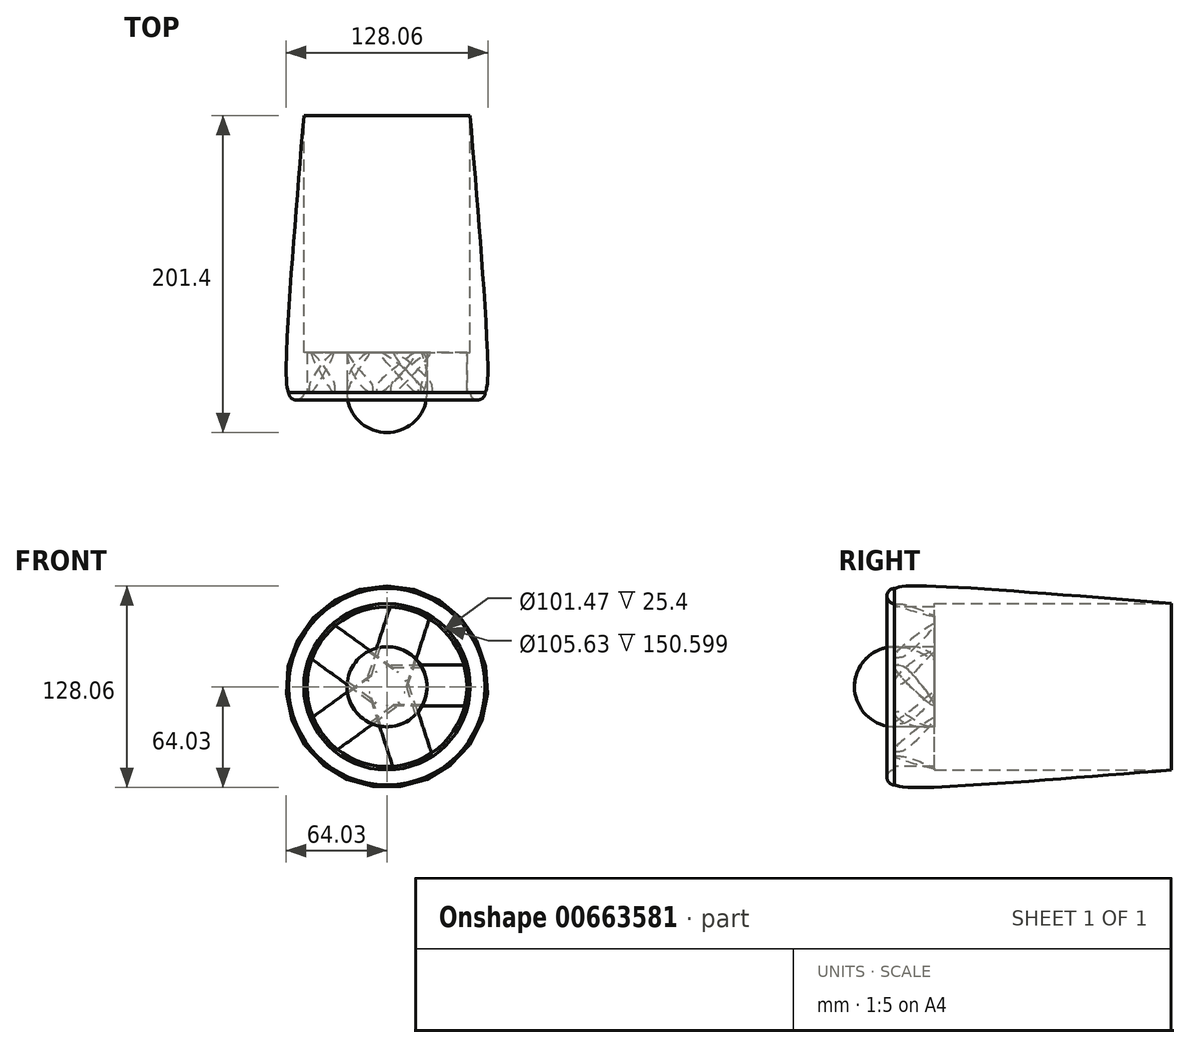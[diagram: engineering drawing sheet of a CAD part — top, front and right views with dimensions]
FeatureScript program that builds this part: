
annotation { "Feature Type Name" : "Feature", "Feature Type Description" : "" }
export const myFeature = defineFeature(function(context is Context, id is Id, definition is map)
    precondition{}
    {
        {
            var Q0;
            Q0=qCreatedBy(makeId("Front.planeOp"),FACE);
            var sketch = newSketch(context, id + "F0", { "sketchPlane" : qUnion([Q0])});
            skCircle(sketch, "E0", {"center": v(0, 0) * mm, "radius": 25.4 * mm});
            skSolve(sketch);
        }
        {
            var Q0;
            Q0 = qSketchRegion(id + "F0", true);
            extrude(context, id + "F1", {"entities" : qUnion([Q0]), "oppositeDirection" : true, "depth" : 25.4 * mm, "offsetDistance" : 25.4 * mm});
        }
        {
            var Q0;
            Q0=qCreatedBy(makeId("Right.planeOp"),FACE);
            var sketch = newSketch(context, id + "F2", { "sketchPlane" : qUnion([Q0])});
            skLineSegment(sketch, "E1", {"start": v(-7.86, -12.08) * mm, "end": v(25.4, -12.08) * mm, "construction": true});
            skLineSegment(sketch, "E2", {"start": v(25.4, -12.08) * mm, "end": v(1.25, 12.07) * mm, "construction": true});
            skLineSegment(sketch, "E3", {"start": v(1.25, 12.07) * mm, "end": v(1.25, -12.08) * mm, "construction": true});
            skFitSpline(sketch, "E4", {"points": [v(0, 13.64) * mm, v(2.87, 13.72) * mm, v(7.87, 11.5) * mm, v(25.4, -12.08) * mm, v(2.79, 7.92) * mm, v(0, 13.64) * mm]});
            skSolve(sketch);
        }
        {
            var Q0;
            Q0 = qSketchRegion(id + "F2", true);
            extrude(context, id + "F3", {"entities" : qUnion([Q0]), "operationType" : NewBodyOperationType.ADD, "depth" : 50.8 * mm, "offsetDistance" : 25.4 * mm});
        }
        {
            var Q0;
            Q0=makeQuery(id+"F1.opExtrude","SWEPT_BODY",BODY,{"disambiguationData":[OSD([sQuery(id+"F0.wireOp",EDGE,"E0")])]});
            var Q1;
            Q1=makeQuery(id+"F1.opExtrude","SWEPT_FACE",FACE,{"disambiguationData":[OSD([sQuery(id+"F0.wireOp",EDGE,"E0")])]});
            circularPattern(context, id + "F4", {"entities" : qUnion([Q0]), "axis" : qUnion([Q1]), "angle" : 360 * degree, "instanceCount" : 5, "equalSpace" : true});
        }
        {
            var Q0;
            Q0=makeQuery(id+"F4.opPattern","COPY",FACE,{"derivedFrom":makeQuery(id+"F1.opExtrude","CAP_FACE",FACE,{"disambiguationData":[OSD([sQuery(id+"F0.wireOp",EDGE,"E0")])],"isStart":true}),"instanceName":"4"});
            var sketch = newSketch(context, id + "F5", { "sketchPlane" : qUnion([Q0])});
            skCircle(sketch, "E5", {"center": v(0, 0) * mm, "radius": 50.74 * mm});
            skCircle(sketch, "E6", {"center": v(0, 0) * mm, "radius": 52.9 * mm});
            skSolve(sketch);
        }
        {
            var Q0;
            Q0 = qSketchRegion(id + "F5", true);
            extrude(context, id + "F6", {"entities" : qUnion([Q0]), "oppositeDirection" : true, "depth" : 25.4 * mm, "offsetDistance" : 25.4 * mm});
        }
        {
            var Q0;
            Q0=qCreatedBy(makeId("Right.planeOp"),FACE);
            var sketch = newSketch(context, id + "F7", { "sketchPlane" : qUnion([Q0])});
            skArc(sketch, "E7", {"start": v(0, 25.4) * mm, "mid": v(-17.96, 17.96) * mm, "end": v(-25.4, 0) * mm});
            skLineSegment(sketch, "E8", {"start": v(0, 0) * mm, "end": v(-25.4, 0) * mm});
            skLineSegment(sketch, "E9", {"start": v(0, 0) * mm, "end": v(0, 25.4) * mm});
            skSolve(sketch);
        }
        {
            var Q0;
            Q0 = qSketchRegion(id + "F7", true);
            var Q1;
            Q1=makeQuery(id+"F4.opPattern","COPY",FACE,{"derivedFrom":makeQuery(id+"F1.opExtrude","SWEPT_FACE",FACE,{"disambiguationData":[OSD([sQuery(id+"F0.wireOp",EDGE,"E0")])]}),"instanceName":"3"});
            revolve(context, id + "F8", {"entities" : qUnion([Q0]), "axis" : qUnion([Q1]), "revolveType" : RevolveType.FULL});
        }
        {
            var Q0;
            Q0=qCreatedBy(makeId("Right.planeOp"),FACE);
            var sketch = newSketch(context, id + "F9", { "sketchPlane" : qUnion([Q0])});
            skLineSegment(sketch, "E10", {"start": v(0, 0) * mm, "end": v(0, 66.43) * mm, "construction": true});
            skCircle(sketch, "E11", {"center": v(0, 57.61) * mm, "radius": 4.8 * mm});
            skLineSegment(sketch, "E12", {"start": v(0, 52.82) * mm, "end": v(176, 52.82) * mm});
            skFitSpline(sketch, "E13", {"points": [v(0, 62.4) * mm, v(7.19, 63.86) * mm, v(176, 52.82) * mm], "startDerivative": vector(27.73, 10.3) * mm, "endDerivative": vector(271.1, -22.35) * mm});
            skSolve(sketch);
        }
        {
            var Q0;
            {var subQ0=sQuery(id+"F9.wireOp",EDGE,"E11");var subQ1=makeQuery(id+"F9.imprint","INTERSECT",VERTEX,{"derivedFrom":[subQ0,sQuery(id+"F9.wireOp",EDGE,"E12")]});Q0=makeQuery(id+"F9.imprint","IMPRINT",FACE,{"disambiguationData":[TD([[makeQuery(id+"F9.imprint","IMPRINT",EDGE,{"disambiguationData":[TD([[subQ1,1.0]])],"derivedFrom":subQ0}),1.0]])]});}
            var Q1;
            {var subQ0=sQuery(id+"F9.wireOp",EDGE,"E12");Q1=makeQuery(id+"F9.imprint","IMPRINT",FACE,{"disambiguationData":[TD([[makeQuery(id+"F9.imprint","IMPRINT",EDGE,{"derivedFrom":subQ0}),1.0]])]});}
            var Q2;
            Q2=makeQuery(id+"F4.opPattern","COPY",FACE,{"derivedFrom":makeQuery(id+"F1.opExtrude","SWEPT_FACE",FACE,{"disambiguationData":[OSD([sQuery(id+"F0.wireOp",EDGE,"E0")])]}),"instanceName":"2"});
            revolve(context, id + "F10", {"operationType" : NewBodyOperationType.ADD, "entities" : qUnion([Q0, Q1]), "axis" : qUnion([Q2]), "revolveType" : RevolveType.FULL});
        }
    });
